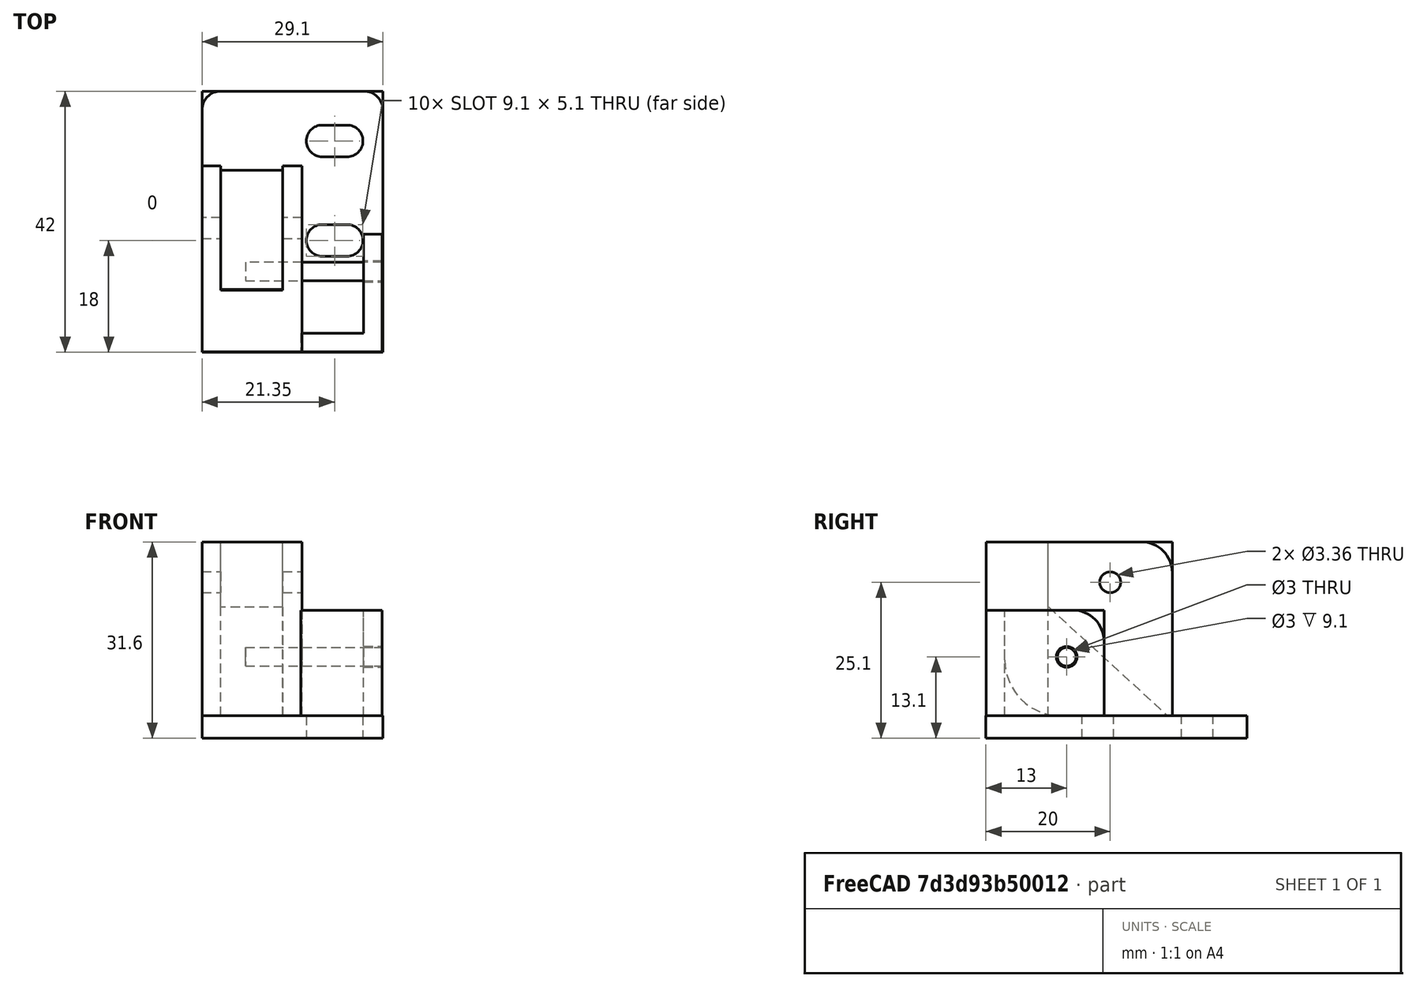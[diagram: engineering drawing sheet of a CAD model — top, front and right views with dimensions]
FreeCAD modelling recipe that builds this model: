
FCSTD DOCUMENT  (FreeCAD 0.16R6706 (Git))
Label: belt-junction r
License: All rights reserved
LicenseURL: http://en.wikipedia.org/wiki/All_rights_reserved
objects: Sketcher::SketchObject×7, PartDesign::Pocket×4, PartDesign::Fillet×3, PartDesign::Pad×3, Mesh::Feature×2, Part::Box×1, PartDesign::Draft×1
note: 26 computed .brp shape members not serialized (recipe doc carries the construction recipe); baked Part::Feature solids carry a one-line shape summary decoded from their .brp

FEATURE [Part::Box] Box  label="Cube"
  Height = 3.6
  Length = 29.1
  Width = 42
FEATURE [Sketcher::SketchObject] Sketch001  label="mnt holes"
  Placement = pos=(0,0,0) rot=(1,0,0;3.14159rad)
  Support = -> Box [Face5]
  sketch-geometry (8):
    g0: ArcOfCircle CenterX=23.35 CenterY=-34 CenterZ=0 NormalX=0 NormalY=0 NormalZ=1 Radius=2.55 StartAngle=4.71239 EndAngle=7.85398
    g1: ArcOfCircle CenterX=19.35 CenterY=-34 CenterZ=0 NormalX=0 NormalY=0 NormalZ=1 Radius=2.55 StartAngle=1.5708 EndAngle=4.71239
    g2: LineSegment StartX=23.35 StartY=-31.45 StartZ=0 EndX=19.35 EndY=-31.45 EndZ=0
    g3: LineSegment StartX=23.35 StartY=-36.55 StartZ=0 EndX=19.35 EndY=-36.55 EndZ=0
    g4: ArcOfCircle CenterX=23.35 CenterY=-18 CenterZ=0 NormalX=0 NormalY=0 NormalZ=1 Radius=2.55 StartAngle=4.71239 EndAngle=7.85398
    g5: ArcOfCircle CenterX=19.35 CenterY=-18 CenterZ=0 NormalX=0 NormalY=0 NormalZ=1 Radius=2.55 StartAngle=1.5708 EndAngle=4.71239
    g6: LineSegment StartX=23.35 StartY=-15.45 StartZ=0 EndX=19.35 EndY=-15.45 EndZ=0
    g7: LineSegment StartX=23.35 StartY=-20.55 StartZ=0 EndX=19.35 EndY=-20.55 EndZ=0
  constraints (20):
    c: Tangent(g0,g3) = 1.5708
    c: Tangent(g0,g2) = -1.5708
    c: Tangent(g2,g1) = -1.5708
    c: Tangent(g3,g1) = 1.5708
    c: Horizontal(g2)
    c: Equal(g0,g1)
    c: Tangent(g4,g7) = 1.5708
    c: Tangent(g4,g6) = -1.5708
    c: Tangent(g6,g5) = -1.5708
    c: Tangent(g7,g5) = 1.5708
    c: Horizontal(g6)
    c: Equal(g4,g5)
    c: Distance(g4,g4) = 5.1
    c: DistanceY(g-1,g5) = -18
    c: DistanceX(g-2,g5) = 19.35
    c: Distance(g4,g5) = 4
    c: Distance(g0,g1) = 4
    c: Distance(g0,g0) = 5.1
    c: DistanceX(g-2,g1) = 19.35
    c: Distance(g0,g4) = 16
FEATURE [PartDesign::Pocket] Pocket
  Length = 5
  Sketch = -> Sketch001
  Type = 0
FEATURE [PartDesign::Fillet] Fillet
  Base = -> Pocket [Edge19,Edge3]
  Radius = 3
FEATURE [Sketcher::SketchObject] Sketch003  label="top pad"
  Placement = pos=(0,0,3.6) rot=(0,0,1;0rad)
  Support = -> Fillet [Face2]
  sketch-geometry (6):
    g0: LineSegment StartX=29 StartY=0.05 StartZ=0 EndX=29 EndY=19 EndZ=0
    g1: LineSegment StartX=29 StartY=19 StartZ=0 EndX=26 EndY=19 EndZ=0
    g2: LineSegment StartX=26 StartY=19 StartZ=0 EndX=26 EndY=3.05 EndZ=0
    g3: LineSegment StartX=26 StartY=3.05 StartZ=0 EndX=15.9 EndY=3.05 EndZ=0
    g4: LineSegment StartX=15.9 StartY=3.05 StartZ=0 EndX=15.9 EndY=0.05 EndZ=0
    g5: LineSegment StartX=15.9 StartY=0.05 StartZ=0 EndX=29 EndY=0.05 EndZ=0
  constraints (19):
    c: Coincident(g0,g1)
    c: Coincident(g1,g2)
    c: Coincident(g2,g3)
    c: Coincident(g3,g4)
    c: Coincident(g4,g5)
    c: Coincident(g5,g0)
    c: Distance(g0,g1) = 3
    c: Equal(g1,g4)
    c: Equal(g1,g4)
    c: Perpendicular(g2,g3)
    c: Parallel(g0,g2)
    c: Parallel(g5,g3)
    c: Parallel(g3,g-1)
    c: Parallel(g2,g4)
    c: DistanceY(g0) = 0.05
    c: Parallel(g1,g-1)
    c: DistanceX(g1) = 26
    c: DistanceY(g0) = 19
    c: DistanceX(g3) = 15.9
FEATURE [PartDesign::Pad] Pad
  Length = 17
  Length2 = 100
  Sketch = -> Sketch003
  Type = 0
FEATURE [Sketcher::SketchObject] Sketch  label="btm pad"
  Placement = pos=(0,0,3.6) rot=(0,0,1;0rad)
  Support = -> Pad [Face8]
  sketch-geometry (8):
    g0: LineSegment StartX=0 StartY=0.05 StartZ=0 EndX=16.1 EndY=0.05 EndZ=0
    g1: LineSegment StartX=16.1 StartY=0.05 StartZ=0 EndX=16.1 EndY=30 EndZ=0
    g2: LineSegment StartX=16.1 StartY=30 StartZ=0 EndX=13 EndY=30 EndZ=0
    g3: LineSegment StartX=13 StartY=30 StartZ=0 EndX=13 EndY=10 EndZ=0
    g4: LineSegment StartX=13 StartY=10 StartZ=0 EndX=3 EndY=10 EndZ=0
    g5: LineSegment StartX=3 StartY=10 StartZ=0 EndX=3 EndY=30 EndZ=0
    g6: LineSegment StartX=3 StartY=30 StartZ=0 EndX=0 EndY=30 EndZ=0
    g7: LineSegment StartX=0 StartY=30 StartZ=0 EndX=0 EndY=0.05 EndZ=0
  constraints (24):
    c: Coincident(g0,g1)
    c: Coincident(g1,g2)
    c: Coincident(g2,g3)
    c: Coincident(g3,g4)
    c: Coincident(g4,g5)
    c: Coincident(g5,g6)
    c: Coincident(g6,g7)
    c: Coincident(g7,g0)
    c: Parallel(g0,g-1)
    c: Perpendicular(g0,g1)
    c: Parallel(g-2,g7)
    c: DistanceX(g0) = 0
    c: DistanceY(g0) = 0.05
    c: Parallel(g4,g-1)
    c: Parallel(g7,g5)
    c: Parallel(g5,g3)
    c: Parallel(g6,g2)
    c: Parallel(g2,g-1)
    c: Equal(g7,g1)
    c: DistanceY(g1) = 30
    c: Distance(g6) = 3
    c: Distance(g4) = 10
    c: Distance(g2,g1) = 3.1
    c: DistanceY(g3) = 10
FEATURE [PartDesign::Pad] Pad001
  Length = 28
  Length2 = 100
  Sketch = -> Sketch
  Type = 0
FEATURE [PartDesign::Fillet] Fillet001
  Base = -> Pad001 [Edge13]
  Radius = 9
FEATURE [Mesh::Feature] davebot_initial_layout  label="btm pulley"
  Placement = pos=(11.5,194.2,-120.1) rot=(0,1,0;1.5708rad)
FEATURE [Mesh::Feature] davebot_initial_layout001  label="top pulley"
  Placement = pos=(24.5,187.2,-132.1) rot=(0,1,0;1.5708rad)
FEATURE [Sketcher::SketchObject] Sketch005
  Placement = pos=(0,0,3.6) rot=(0,0,1;0rad)
  Support = -> Fillet001 [Face1]
  sketch-geometry (4):
    g0: LineSegment StartX=2.01266 StartY=9.26857 StartZ=0 EndX=14.2218 EndY=9.26857 EndZ=0
    g1: LineSegment StartX=14.2218 StartY=9.26857 StartZ=0 EndX=14.2218 EndY=29.272 EndZ=0
    g2: LineSegment StartX=14.2218 StartY=29.272 StartZ=0 EndX=2.01266 EndY=29.272 EndZ=0
    g3: LineSegment StartX=2.01266 StartY=29.272 StartZ=0 EndX=2.01266 EndY=9.26857 EndZ=0
  constraints (8):
    c: Coincident(g0,g1)
    c: Coincident(g1,g2)
    c: Coincident(g2,g3)
    c: Coincident(g3,g0)
    c: Horizontal(g0)
    c: Horizontal(g2)
    c: Vertical(g1)
    c: Vertical(g3)
FEATURE [PartDesign::Pad] Pad002
  Length = 17.5
  Length2 = 100
  Sketch = -> Sketch005
  Type = 0
FEATURE [PartDesign::Draft] Draft
  Angle = 47.6
  Base = -> Pad002 [Face10]
  NeutralPlane = -> Pad002 [Face3]
FEATURE [Sketcher::SketchObject] Sketch002  label="axel hole"
  Placement = pos=(29,0,0) rot=(0.57735,0.57735,0.57735;2.0944rad)
  Support = -> Draft [Face22]
  sketch-geometry (1):
    g0: Circle CenterX=13 CenterY=13.1 CenterZ=0 NormalX=0 NormalY=0 NormalZ=1 Radius=1.5
  constraints (3):
    c: Radius(g0) = 1.5
    c: DistanceY(g-1,g0) = 13.1
    c: DistanceX(g-2,g0) = 13
FEATURE [PartDesign::Pocket] Pocket001
  Length = 22
  Sketch = -> Sketch002
  Type = 0
FEATURE [Sketcher::SketchObject] Sketch004  label="btm axel hole"
  Placement = pos=(16.1,0,0) rot=(0.57735,0.57735,0.57735;2.0944rad)
  Support = -> Pocket001 [Face5]
  sketch-geometry (1):
    g0: Circle CenterX=20 CenterY=25.1 CenterZ=0 NormalX=0 NormalY=0 NormalZ=1 Radius=1.68
  constraints (3):
    c: DistanceX(g0) = 20
    c: DistanceY(g0) = 25.1
    c: Radius(g0) = 1.68
FEATURE [PartDesign::Pocket] Pocket002
  Length = 18
  Sketch = -> Sketch004
  Type = 0
FEATURE [PartDesign::Fillet] Fillet002
  Base = -> Pocket002 [Edge64,Edge50,Edge45]
  Radius = 5
FEATURE [Sketcher::SketchObject] Sketch006
  Placement = pos=(29,0,0) rot=(0.57735,0.57735,0.57735;2.0944rad)
  Support = -> Fillet002 [Face9]
  sketch-geometry (1):
    g0: Circle CenterX=13 CenterY=13.1 CenterZ=0 NormalX=0 NormalY=0 NormalZ=1 Radius=1.68
  constraints (3):
    c: Radius(g0) = 1.68
    c: DistanceY(g0) = 13.1
    c: DistanceX(g0) = 13
FEATURE [PartDesign::Pocket] Pocket003
  Length = 3
  Sketch = -> Sketch006
  Type = 0
